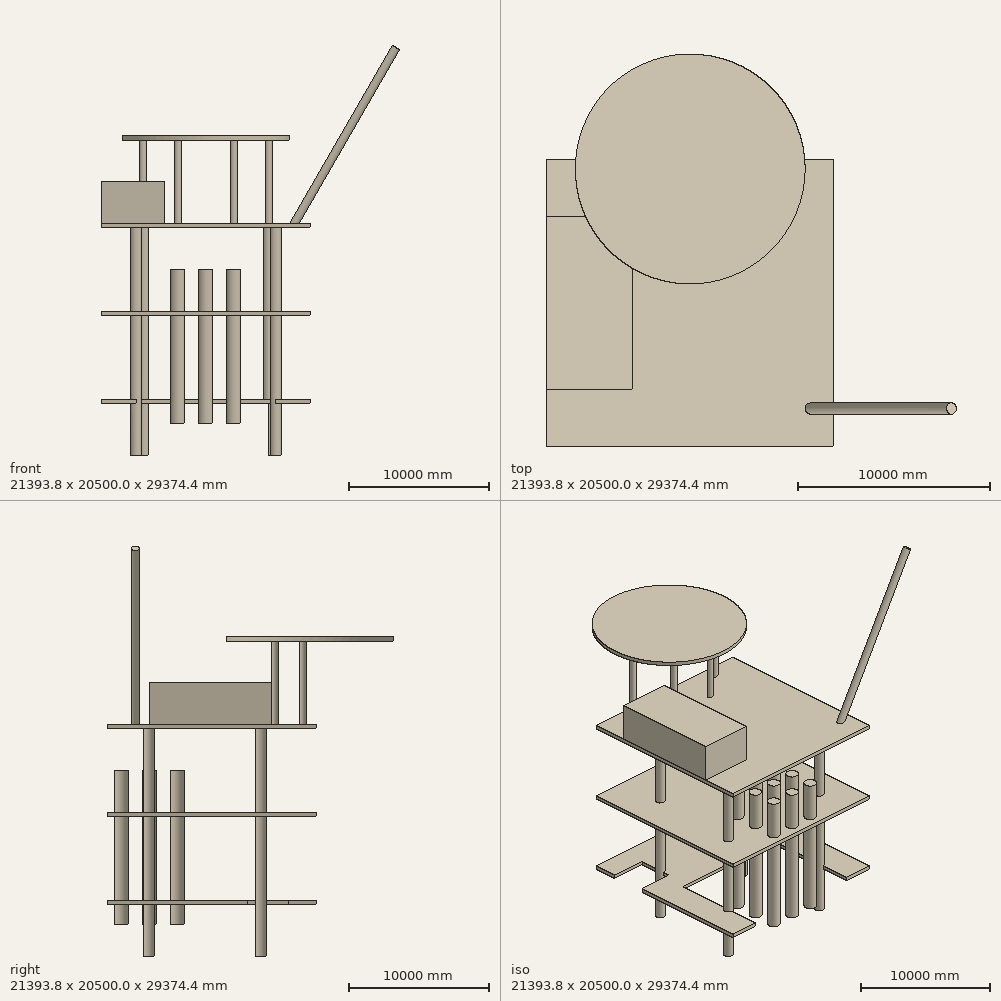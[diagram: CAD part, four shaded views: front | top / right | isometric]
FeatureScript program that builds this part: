
annotation { "Feature Type Name" : "Feature", "Feature Type Description" : "" }
export const myFeature = defineFeature(function(context is Context, id is Id, definition is map)
    precondition{}
    {
        {
            var Q0;
            Q0=qCreatedBy(makeId("Top.planeOp"),FACE);
            var sketch = newSketch(context, id + "F0", { "sketchPlane" : qUnion([Q0])});
            skLineSegment(sketch, "E0.bottom", {"start": v(-8810.08, 6724.82) * mm, "end": v(6189.92, 6724.82) * mm});
            skLineSegment(sketch, "E0.top", {"start": v(-8810.08, 21724.82) * mm, "end": v(6189.92, 21724.82) * mm});
            skLineSegment(sketch, "E0.left", {"start": v(-8810.08, 6724.82) * mm, "end": v(-8810.08, 21724.82) * mm});
            skLineSegment(sketch, "E0.right", {"start": v(6189.92, 6724.82) * mm, "end": v(6189.92, 21724.82) * mm});
            skSolve(sketch);
        }
        {
            var Q0;
            Q0 = qSketchRegion(id + "F0", true);
            extrude(context, id + "F1", {"entities" : qUnion([Q0]), "oppositeDirection" : true, "depth" : 300 * mm, "offsetDistance" : 25 * mm});
        }
        {
            var Q0;
            Q0=makeQuery(id+"F1.opExtrude","CAP_FACE",FACE,{"disambiguationData":[OSD([sQuery(id+"F0.wireOp",EDGE,"E0.bottom"),sQuery(id+"F0.wireOp",EDGE,"E0.top"),sQuery(id+"F0.wireOp",EDGE,"E0.left"),sQuery(id+"F0.wireOp",EDGE,"E0.right")])],"isStart":true});
            var sketch = newSketch(context, id + "F2", { "sketchPlane" : qUnion([Q0])});
            skLineSegment(sketch, "E1", {"start": v(-6310.08, 6724.82) * mm, "end": v(-6310.08, 14724.82) * mm});
            skLineSegment(sketch, "E2", {"start": v(-6310.08, 14724.82) * mm, "end": v(3689.92, 14724.82) * mm});
            skLineSegment(sketch, "E3", {"start": v(3689.92, 14724.82) * mm, "end": v(3689.92, 6724.82) * mm});
            skLineSegment(sketch, "E4", {"start": v(-1310.08, 6724.82) * mm, "end": v(-1310.08, 14724.82) * mm, "construction": true});
            skSolve(sketch);
        }
        {
            var Q0;
            Q0 = qSketchRegion(id + "F2", true);
            var Q1;
            {var subQ0=sQuery(id+"F2.wireOp",EDGE,"E1");Q1=makeQuery(id+"F2.imprint","IMPRINT",FACE,{"disambiguationData":[TD([[makeQuery(id+"F2.imprint","IMPRINT",EDGE,{"derivedFrom":subQ0}),-1.0]])]});}
            extrude(context, id + "F3", {"entities" : qUnion([Q0, Q1]), "operationType" : NewBodyOperationType.REMOVE, "endBound" : BoundingType.THROUGH_ALL, "oppositeDirection" : true, "depth" : 25 * mm, "offsetDistance" : 25 * mm});
        }
        {
            var Q0;
            Q0=makeQuery(id+"F1.opExtrude","CAP_FACE",FACE,{"disambiguationData":[OSD([sQuery(id+"F0.wireOp",EDGE,"E0.bottom"),sQuery(id+"F0.wireOp",EDGE,"E0.top"),sQuery(id+"F0.wireOp",EDGE,"E0.left"),sQuery(id+"F0.wireOp",EDGE,"E0.right")])],"isStart":true});
            var sketch = newSketch(context, id + "F4", { "sketchPlane" : qUnion([Q0])});
            skLineSegment(sketch, "E5", {"start": v(-8810.08, 19724.82) * mm, "end": v(-5810.08, 19724.82) * mm});
            skLineSegment(sketch, "E6", {"start": v(-5810.08, 19724.82) * mm, "end": v(-5810.08, 16724.82) * mm});
            skLineSegment(sketch, "E7", {"start": v(-5810.08, 16724.82) * mm, "end": v(-8810.08, 16724.82) * mm});
            skLineSegment(sketch, "E8", {"start": v(6189.92, 19724.82) * mm, "end": v(3189.92, 19724.82) * mm});
            skLineSegment(sketch, "E9", {"start": v(3189.92, 19724.82) * mm, "end": v(3189.92, 16724.82) * mm});
            skLineSegment(sketch, "E10", {"start": v(3189.92, 16724.82) * mm, "end": v(6189.92, 16724.82) * mm});
            skSolve(sketch);
        }
        {
            var Q0;
            {var subQ0=sQuery(id+"F4.wireOp",EDGE,"E5");Q0=makeQuery(id+"F4.imprint","IMPRINT",FACE,{"disambiguationData":[TD([[makeQuery(id+"F4.imprint","IMPRINT",EDGE,{"derivedFrom":subQ0}),-1.0]])]});}
            var Q1;
            {var subQ0=sQuery(id+"F4.wireOp",EDGE,"E8");Q1=makeQuery(id+"F4.imprint","IMPRINT",FACE,{"disambiguationData":[TD([[makeQuery(id+"F4.imprint","IMPRINT",EDGE,{"derivedFrom":subQ0}),1.0]])]});}
            extrude(context, id + "F5", {"entities" : qUnion([Q0, Q1]), "operationType" : NewBodyOperationType.REMOVE, "endBound" : BoundingType.THROUGH_ALL, "oppositeDirection" : true, "depth" : 25 * mm, "offsetDistance" : 25 * mm});
        }
        {
            var Q0;
            Q0=makeQuery(id+"F1.opExtrude","CAP_FACE",FACE,{"disambiguationData":[OSD([sQuery(id+"F0.wireOp",EDGE,"E0.bottom"),sQuery(id+"F0.wireOp",EDGE,"E0.top"),sQuery(id+"F0.wireOp",EDGE,"E0.left"),sQuery(id+"F0.wireOp",EDGE,"E0.right")])],"isStart":true});
            var sketch = newSketch(context, id + "F6", { "sketchPlane" : qUnion([Q0])});
            skCircle(sketch, "E11", {"center": v(-5810.08, 17724.82) * mm, "radius": 400 * mm});
            skCircle(sketch, "E12", {"center": v(3189.92, 17724.82) * mm, "radius": 400 * mm});
            skCircle(sketch, "E13", {"center": v(-6310.08, 9724.82) * mm, "radius": 400 * mm});
            skCircle(sketch, "E14", {"center": v(3689.92, 9724.82) * mm, "radius": 400 * mm});
            skSolve(sketch);
        }
        {
            var Q0;
            {var subQ0=sQuery(id+"F6.wireOp",EDGE,"E11");var subQ1=makeQuery(id+"F5.boolean.opBoolean","COPY",EDGE,{"derivedFrom":makeQuery(id+"F5.opExtrude","CAP_EDGE",EDGE,{"disambiguationData":[OSD([sQuery(id+"F4.wireOp",EDGE,"E6")])],"isStart":true})});var subQ2=makeQuery(id+"F6.imprint","INTERSECT",VERTEX,{"disambiguationData":[OD(0.0)],"derivedFrom":[subQ1,subQ0]});Q0=makeQuery(id+"F6.imprint","IMPRINT",FACE,{"disambiguationData":[TD([[makeQuery(id+"F6.imprint","IMPRINT",EDGE,{"disambiguationData":[TD([[subQ2,-1.0]])],"derivedFrom":subQ0}),1.0]])]});}
            var Q1;
            {var subQ0=sQuery(id+"F6.wireOp",EDGE,"E11");var subQ1=makeQuery(id+"F5.boolean.opBoolean","COPY",EDGE,{"derivedFrom":makeQuery(id+"F5.opExtrude","CAP_EDGE",EDGE,{"disambiguationData":[OSD([sQuery(id+"F4.wireOp",EDGE,"E6")])],"isStart":true})});var subQ2=makeQuery(id+"F6.imprint","INTERSECT",VERTEX,{"disambiguationData":[OD(0.0)],"derivedFrom":[subQ1,subQ0]});Q1=makeQuery(id+"F6.imprint","IMPRINT",FACE,{"disambiguationData":[TD([[makeQuery(id+"F6.imprint","IMPRINT",EDGE,{"disambiguationData":[TD([[subQ2,1.0]])],"derivedFrom":subQ0}),1.0]])]});}
            var Q2;
            {var subQ0=sQuery(id+"F6.wireOp",EDGE,"E13");var subQ1=makeQuery(id+"F3.boolean.opBoolean","COPY",EDGE,{"derivedFrom":makeQuery(id+"F3.opExtrude","CAP_EDGE",EDGE,{"disambiguationData":[OSD([sQuery(id+"F2.wireOp",EDGE,"E1")])],"isStart":true})});var subQ2=makeQuery(id+"F6.imprint","INTERSECT",VERTEX,{"disambiguationData":[OD(0.0)],"derivedFrom":[subQ1,subQ0]});Q2=makeQuery(id+"F6.imprint","IMPRINT",FACE,{"disambiguationData":[TD([[makeQuery(id+"F6.imprint","IMPRINT",EDGE,{"disambiguationData":[TD([[subQ2,-1.0]])],"derivedFrom":subQ0}),1.0]])]});}
            var Q3;
            {var subQ0=sQuery(id+"F6.wireOp",EDGE,"E13");var subQ1=makeQuery(id+"F3.boolean.opBoolean","COPY",EDGE,{"derivedFrom":makeQuery(id+"F3.opExtrude","CAP_EDGE",EDGE,{"disambiguationData":[OSD([sQuery(id+"F2.wireOp",EDGE,"E1")])],"isStart":true})});var subQ2=makeQuery(id+"F6.imprint","INTERSECT",VERTEX,{"disambiguationData":[OD(0.0)],"derivedFrom":[subQ1,subQ0]});Q3=makeQuery(id+"F6.imprint","IMPRINT",FACE,{"disambiguationData":[TD([[makeQuery(id+"F6.imprint","IMPRINT",EDGE,{"disambiguationData":[TD([[subQ2,1.0]])],"derivedFrom":subQ0}),1.0]])]});}
            var Q4;
            {var subQ0=sQuery(id+"F6.wireOp",EDGE,"E12");var subQ1=makeQuery(id+"F5.boolean.opBoolean","COPY",EDGE,{"derivedFrom":makeQuery(id+"F5.opExtrude","CAP_EDGE",EDGE,{"disambiguationData":[OSD([sQuery(id+"F4.wireOp",EDGE,"E9")])],"isStart":true})});var subQ2=makeQuery(id+"F6.imprint","INTERSECT",VERTEX,{"disambiguationData":[OD(0.0)],"derivedFrom":[subQ1,subQ0]});Q4=makeQuery(id+"F6.imprint","IMPRINT",FACE,{"disambiguationData":[TD([[makeQuery(id+"F6.imprint","IMPRINT",EDGE,{"disambiguationData":[TD([[subQ2,1.0]])],"derivedFrom":subQ0}),1.0]])]});}
            var Q5;
            {var subQ0=sQuery(id+"F6.wireOp",EDGE,"E12");var subQ1=makeQuery(id+"F5.boolean.opBoolean","COPY",EDGE,{"derivedFrom":makeQuery(id+"F5.opExtrude","CAP_EDGE",EDGE,{"disambiguationData":[OSD([sQuery(id+"F4.wireOp",EDGE,"E9")])],"isStart":true})});var subQ2=makeQuery(id+"F6.imprint","INTERSECT",VERTEX,{"disambiguationData":[OD(0.0)],"derivedFrom":[subQ1,subQ0]});Q5=makeQuery(id+"F6.imprint","IMPRINT",FACE,{"disambiguationData":[TD([[makeQuery(id+"F6.imprint","IMPRINT",EDGE,{"disambiguationData":[TD([[subQ2,-1.0]])],"derivedFrom":subQ0}),1.0]])]});}
            var Q6;
            {var subQ0=sQuery(id+"F6.wireOp",EDGE,"E14");var subQ1=makeQuery(id+"F3.boolean.opBoolean","COPY",EDGE,{"derivedFrom":makeQuery(id+"F3.opExtrude","CAP_EDGE",EDGE,{"disambiguationData":[OSD([sQuery(id+"F2.wireOp",EDGE,"E3")])],"isStart":true})});var subQ2=makeQuery(id+"F6.imprint","INTERSECT",VERTEX,{"disambiguationData":[OD(0.0)],"derivedFrom":[subQ1,subQ0]});Q6=makeQuery(id+"F6.imprint","IMPRINT",FACE,{"disambiguationData":[TD([[makeQuery(id+"F6.imprint","IMPRINT",EDGE,{"disambiguationData":[TD([[subQ2,-1.0]])],"derivedFrom":subQ0}),1.0]])]});}
            var Q7;
            {var subQ0=sQuery(id+"F6.wireOp",EDGE,"E14");var subQ1=makeQuery(id+"F3.boolean.opBoolean","COPY",EDGE,{"derivedFrom":makeQuery(id+"F3.opExtrude","CAP_EDGE",EDGE,{"disambiguationData":[OSD([sQuery(id+"F2.wireOp",EDGE,"E3")])],"isStart":true})});var subQ2=makeQuery(id+"F6.imprint","INTERSECT",VERTEX,{"disambiguationData":[OD(0.0)],"derivedFrom":[subQ1,subQ0]});Q7=makeQuery(id+"F6.imprint","IMPRINT",FACE,{"disambiguationData":[TD([[makeQuery(id+"F6.imprint","IMPRINT",EDGE,{"disambiguationData":[TD([[subQ2,1.0]])],"derivedFrom":subQ0}),1.0]])]});}
            extrude(context, id + "F7", {"entities" : qUnion([Q0, Q1, Q2, Q3, Q4, Q5, Q6, Q7]), "operationType" : NewBodyOperationType.ADD, "depth" : 6000 * mm, "offsetDistance" : 25 * mm});
        }
        {
            var Q0;
            Q0=makeQuery(id+"F7.opExtrude","CAP_FACE",FACE,{"disambiguationData":[OSD([sQuery(id+"F6.wireOp",EDGE,"E12")])],"isStart":true});
            var sketch = newSketch(context, id + "F8", { "sketchPlane" : qUnion([Q0])});
            skCircle(sketch, "E15", {"center": v(-6310.08, -9724.82) * mm, "radius": 400 * mm});
            skCircle(sketch, "E16", {"center": v(3689.92, -9724.82) * mm, "radius": 400 * mm});
            skCircle(sketch, "E17", {"center": v(-5810.08, -17724.82) * mm, "radius": 400 * mm});
            skCircle(sketch, "E18", {"center": v(3189.92, -17724.82) * mm, "radius": 400 * mm});
            skSolve(sketch);
        }
        {
            var Q0;
            Q0=makeQuery(id+"F8.imprint","IMPRINT",FACE,{"disambiguationData":[TD([[makeQuery(id+"F8.imprint","IMPRINT",EDGE,{"derivedFrom":sQuery(id+"F8.wireOp",EDGE,"E17")}),1.0]])]});
            var Q1;
            Q1=makeQuery(id+"F8.imprint","IMPRINT",FACE,{"disambiguationData":[TD([[makeQuery(id+"F8.imprint","IMPRINT",EDGE,{"disambiguationData":[OD(1.0)],"derivedFrom":sQuery(id+"F8.wireOp",EDGE,"E18")}),-1.0]])]});
            var Q2;
            Q2=makeQuery(id+"F8.imprint","IMPRINT",FACE,{"disambiguationData":[TD([[makeQuery(id+"F8.imprint","IMPRINT",EDGE,{"derivedFrom":sQuery(id+"F8.wireOp",EDGE,"E15")}),1.0]])]});
            var Q3;
            Q3=makeQuery(id+"F8.imprint","IMPRINT",FACE,{"disambiguationData":[TD([[makeQuery(id+"F8.imprint","IMPRINT",EDGE,{"derivedFrom":sQuery(id+"F8.wireOp",EDGE,"E16")}),1.0]])]});
            extrude(context, id + "F9", {"entities" : qUnion([Q0, Q1, Q2, Q3]), "operationType" : NewBodyOperationType.ADD, "depth" : 4000 * mm, "offsetDistance" : 25 * mm});
        }
        {
            var Q0;
            Q0=makeQuery(id+"F7.opExtrude","CAP_FACE",FACE,{"disambiguationData":[OSD([sQuery(id+"F6.wireOp",EDGE,"E11")])],"isStart":false});
            var sketch = newSketch(context, id + "F10", { "sketchPlane" : qUnion([Q0])});
            skLineSegment(sketch, "E19.bottom", {"start": v(-8810.08, 21724.82) * mm, "end": v(6189.92, 21724.82) * mm});
            skLineSegment(sketch, "E19.top", {"start": v(-8810.08, 6724.82) * mm, "end": v(6189.92, 6724.82) * mm});
            skLineSegment(sketch, "E19.left", {"start": v(-8810.08, 21724.82) * mm, "end": v(-8810.08, 6724.82) * mm});
            skLineSegment(sketch, "E19.right", {"start": v(6189.92, 21724.82) * mm, "end": v(6189.92, 6724.82) * mm});
            skSolve(sketch);
        }
        {
            var Q0;
            Q0=makeQuery(id+"F10.imprint","IMPRINT",FACE,{"disambiguationData":[TD([[makeQuery(id+"F10.imprint","IMPRINT",EDGE,{"derivedFrom":sQuery(id+"F10.wireOp",EDGE,"E19.bottom")}),-1.0]])]});
            var Q1;
            Q1=makeQuery(id+"F10.imprint","IMPRINT",FACE,{"disambiguationData":[TD([[makeQuery(id+"F10.imprint","IMPRINT",EDGE,{"derivedFrom":makeQuery(id+"F7.opExtrude","CAP_EDGE",EDGE,{"disambiguationData":[OSD([sQuery(id+"F6.wireOp",EDGE,"E11")])],"isStart":false})}),1.0]])]});
            extrude(context, id + "F11", {"entities" : qUnion([Q0, Q1]), "operationType" : NewBodyOperationType.ADD, "depth" : 300 * mm, "offsetDistance" : 25 * mm});
        }
        {
            var Q0;
            Q0=makeQuery(id+"F11.opExtrude","CAP_FACE",FACE,{"disambiguationData":[OSD([sQuery(id+"F10.wireOp",EDGE,"E19.bottom"),sQuery(id+"F10.wireOp",EDGE,"E19.top"),sQuery(id+"F10.wireOp",EDGE,"E19.left"),sQuery(id+"F10.wireOp",EDGE,"E19.right")])],"isStart":false});
            var sketch = newSketch(context, id + "F12", { "sketchPlane" : qUnion([Q0])});
            skCircle(sketch, "E20", {"center": v(-3310.08, 7724.82) * mm, "radius": 500 * mm});
            skCircle(sketch, "E21", {"center": v(-1310.08, 7724.82) * mm, "radius": 500 * mm});
            skCircle(sketch, "E22", {"center": v(689.92, 7724.82) * mm, "radius": 500 * mm});
            skCircle(sketch, "E23", {"center": v(-3310.08, 9724.82) * mm, "radius": 500 * mm});
            skCircle(sketch, "E24", {"center": v(-1310.08, 9724.82) * mm, "radius": 500 * mm});
            skCircle(sketch, "E25", {"center": v(689.92, 9724.82) * mm, "radius": 500 * mm});
            skCircle(sketch, "E26", {"center": v(-3310.08, 11724.82) * mm, "radius": 500 * mm});
            skCircle(sketch, "E27", {"center": v(-1310.08, 11724.82) * mm, "radius": 500 * mm});
            skCircle(sketch, "E28", {"center": v(689.92, 11724.82) * mm, "radius": 500 * mm});
            skSolve(sketch);
        }
        {
            var Q0;
            Q0=makeQuery(id+"F12.imprint","IMPRINT",FACE,{"disambiguationData":[TD([[makeQuery(id+"F12.imprint","IMPRINT",EDGE,{"derivedFrom":sQuery(id+"F12.wireOp",EDGE,"E20")}),1.0]])]});
            var Q1;
            Q1=makeQuery(id+"F12.imprint","IMPRINT",FACE,{"disambiguationData":[TD([[makeQuery(id+"F12.imprint","IMPRINT",EDGE,{"derivedFrom":sQuery(id+"F12.wireOp",EDGE,"E23")}),1.0]])]});
            var Q2;
            Q2=makeQuery(id+"F12.imprint","IMPRINT",FACE,{"disambiguationData":[TD([[makeQuery(id+"F12.imprint","IMPRINT",EDGE,{"derivedFrom":sQuery(id+"F12.wireOp",EDGE,"E26")}),1.0]])]});
            var Q3;
            Q3=makeQuery(id+"F12.imprint","IMPRINT",FACE,{"disambiguationData":[TD([[makeQuery(id+"F12.imprint","IMPRINT",EDGE,{"derivedFrom":sQuery(id+"F12.wireOp",EDGE,"E27")}),1.0]])]});
            var Q4;
            Q4=makeQuery(id+"F12.imprint","IMPRINT",FACE,{"disambiguationData":[TD([[makeQuery(id+"F12.imprint","IMPRINT",EDGE,{"derivedFrom":sQuery(id+"F12.wireOp",EDGE,"E28")}),1.0]])]});
            var Q5;
            Q5=makeQuery(id+"F12.imprint","IMPRINT",FACE,{"disambiguationData":[TD([[makeQuery(id+"F12.imprint","IMPRINT",EDGE,{"derivedFrom":sQuery(id+"F12.wireOp",EDGE,"E25")}),1.0]])]});
            var Q6;
            Q6=makeQuery(id+"F12.imprint","IMPRINT",FACE,{"disambiguationData":[TD([[makeQuery(id+"F12.imprint","IMPRINT",EDGE,{"derivedFrom":sQuery(id+"F12.wireOp",EDGE,"E22")}),1.0]])]});
            var Q7;
            Q7=makeQuery(id+"F12.imprint","IMPRINT",FACE,{"disambiguationData":[TD([[makeQuery(id+"F12.imprint","IMPRINT",EDGE,{"derivedFrom":sQuery(id+"F12.wireOp",EDGE,"E21")}),1.0]])]});
            var Q8;
            Q8=makeQuery(id+"F12.imprint","IMPRINT",FACE,{"disambiguationData":[TD([[makeQuery(id+"F12.imprint","IMPRINT",EDGE,{"derivedFrom":sQuery(id+"F12.wireOp",EDGE,"E24")}),1.0]])]});
            extrude(context, id + "F13", {"entities" : qUnion([Q0, Q1, Q2, Q3, Q4, Q5, Q6, Q7, Q8]), "oppositeDirection" : true, "depth" : 8000 * mm, "offsetDistance" : 25 * mm});
        }
        {
            var Q0;
            Q0=makeQuery(id+"F13.opExtrude","CAP_FACE",FACE,{"disambiguationData":[OSD([sQuery(id+"F12.wireOp",EDGE,"E20")])],"isStart":true});
            var Q1;
            Q1=makeQuery(id+"F13.opExtrude","CAP_FACE",FACE,{"disambiguationData":[OSD([sQuery(id+"F12.wireOp",EDGE,"E23")])],"isStart":true});
            var Q2;
            Q2=makeQuery(id+"F13.opExtrude","CAP_FACE",FACE,{"disambiguationData":[OSD([sQuery(id+"F12.wireOp",EDGE,"E26")])],"isStart":true});
            var Q3;
            Q3=makeQuery(id+"F13.opExtrude","CAP_FACE",FACE,{"disambiguationData":[OSD([sQuery(id+"F12.wireOp",EDGE,"E27")])],"isStart":true});
            var Q4;
            Q4=makeQuery(id+"F13.opExtrude","CAP_FACE",FACE,{"disambiguationData":[OSD([sQuery(id+"F12.wireOp",EDGE,"E24")])],"isStart":true});
            var Q5;
            Q5=makeQuery(id+"F13.opExtrude","CAP_FACE",FACE,{"disambiguationData":[OSD([sQuery(id+"F12.wireOp",EDGE,"E21")])],"isStart":true});
            var Q6;
            Q6=makeQuery(id+"F13.opExtrude","CAP_FACE",FACE,{"disambiguationData":[OSD([sQuery(id+"F12.wireOp",EDGE,"E22")])],"isStart":true});
            var Q7;
            Q7=makeQuery(id+"F13.opExtrude","CAP_FACE",FACE,{"disambiguationData":[OSD([sQuery(id+"F12.wireOp",EDGE,"E25")])],"isStart":true});
            var Q8;
            Q8=makeQuery(id+"F13.opExtrude","CAP_FACE",FACE,{"disambiguationData":[OSD([sQuery(id+"F12.wireOp",EDGE,"E28")])],"isStart":true});
            extrude(context, id + "F14", {"entities" : qUnion([Q0, Q1, Q2, Q3, Q4, Q5, Q6, Q7, Q8]), "depth" : 3000 * mm, "offsetDistance" : 25 * mm});
        }
        {
            var Q0;
            Q0=makeQuery(id+"F12.imprint","IMPRINT",FACE,{"disambiguationData":[TD([[makeQuery(id+"F12.imprint","IMPRINT",EDGE,{"derivedFrom":sQuery(id+"F12.wireOp",EDGE,"E20")}),-1.0]])]});
            var sketch = newSketch(context, id + "F15", { "sketchPlane" : qUnion([Q0])});
            skCircle(sketch, "E29", {"center": v(-5810.08, 17724.82) * mm, "radius": 400 * mm});
            skCircle(sketch, "E30", {"center": v(3189.92, 17724.82) * mm, "radius": 400 * mm});
            skCircle(sketch, "E31", {"center": v(-6310.08, 9724.82) * mm, "radius": 400 * mm});
            skCircle(sketch, "E32", {"center": v(3689.92, 9724.82) * mm, "radius": 400 * mm});
            skSolve(sketch);
        }
        {
            var Q0;
            Q0=makeQuery(id+"F15.imprint","IMPRINT",FACE,{"disambiguationData":[TD([[makeQuery(id+"F15.imprint","IMPRINT",EDGE,{"derivedFrom":sQuery(id+"F15.wireOp",EDGE,"E29")}),1.0]])]});
            var Q1;
            Q1=makeQuery(id+"F15.imprint","IMPRINT",FACE,{"disambiguationData":[TD([[makeQuery(id+"F15.imprint","IMPRINT",EDGE,{"derivedFrom":sQuery(id+"F15.wireOp",EDGE,"E30")}),1.0]])]});
            var Q2;
            Q2=makeQuery(id+"F15.imprint","IMPRINT",FACE,{"disambiguationData":[TD([[makeQuery(id+"F15.imprint","IMPRINT",EDGE,{"derivedFrom":sQuery(id+"F15.wireOp",EDGE,"E31")}),1.0]])]});
            var Q3;
            Q3=makeQuery(id+"F15.imprint","IMPRINT",FACE,{"disambiguationData":[TD([[makeQuery(id+"F15.imprint","IMPRINT",EDGE,{"derivedFrom":sQuery(id+"F15.wireOp",EDGE,"E32")}),1.0]])]});
            extrude(context, id + "F16", {"entities" : qUnion([Q0, Q1, Q2, Q3]), "operationType" : NewBodyOperationType.ADD, "depth" : 6000 * mm, "offsetDistance" : 25 * mm});
        }
        {
            var Q0;
            Q0=makeQuery(id+"F16.opExtrude","CAP_FACE",FACE,{"disambiguationData":[OSD([sQuery(id+"F15.wireOp",EDGE,"E31")])],"isStart":false});
            var sketch = newSketch(context, id + "F17", { "sketchPlane" : qUnion([Q0])});
            skLineSegment(sketch, "E33.bottom", {"start": v(-8810.08, 21724.82) * mm, "end": v(6189.92, 21724.82) * mm});
            skLineSegment(sketch, "E33.top", {"start": v(-8810.08, 6724.82) * mm, "end": v(6189.92, 6724.82) * mm});
            skLineSegment(sketch, "E33.left", {"start": v(-8810.08, 21724.82) * mm, "end": v(-8810.08, 6724.82) * mm});
            skLineSegment(sketch, "E33.right", {"start": v(6189.92, 21724.82) * mm, "end": v(6189.92, 6724.82) * mm});
            skSolve(sketch);
        }
        {
            var Q0;
            Q0=makeQuery(id+"F17.imprint","IMPRINT",FACE,{"disambiguationData":[TD([[makeQuery(id+"F17.imprint","IMPRINT",EDGE,{"derivedFrom":sQuery(id+"F17.wireOp",EDGE,"E33.bottom")}),-1.0]])]});
            var Q1;
            Q1=makeQuery(id+"F17.imprint","IMPRINT",FACE,{"disambiguationData":[TD([[makeQuery(id+"F17.imprint","IMPRINT",EDGE,{"derivedFrom":makeQuery(id+"F16.opExtrude","CAP_EDGE",EDGE,{"disambiguationData":[OSD([sQuery(id+"F15.wireOp",EDGE,"E31")])],"isStart":false})}),1.0]])]});
            extrude(context, id + "F18", {"entities" : qUnion([Q0, Q1]), "operationType" : NewBodyOperationType.ADD, "depth" : 300 * mm, "offsetDistance" : 25 * mm});
        }
        {
            var Q0;
            Q0=makeQuery(id+"F18.opExtrude","CAP_FACE",FACE,{"disambiguationData":[OSD([sQuery(id+"F17.wireOp",EDGE,"E33.bottom"),sQuery(id+"F17.wireOp",EDGE,"E33.top"),sQuery(id+"F17.wireOp",EDGE,"E33.left"),sQuery(id+"F17.wireOp",EDGE,"E33.right")])],"isStart":false});
            var sketch = newSketch(context, id + "F19", { "sketchPlane" : qUnion([Q0])});
            skLineSegment(sketch, "E34.bottom", {"start": v(-8810.08, 18724.82) * mm, "end": v(-4310.08, 18724.82) * mm});
            skLineSegment(sketch, "E34.top", {"start": v(-8810.08, 9724.82) * mm, "end": v(-4310.08, 9724.82) * mm});
            skLineSegment(sketch, "E34.left", {"start": v(-8810.08, 18724.82) * mm, "end": v(-8810.08, 9724.82) * mm});
            skLineSegment(sketch, "E34.right", {"start": v(-4310.08, 18724.82) * mm, "end": v(-4310.08, 9724.82) * mm});
            skCircle(sketch, "E35", {"center": v(-3310.08, 18724.82) * mm, "radius": 250 * mm});
            skCircle(sketch, "E36", {"center": v(689.92, 18724.82) * mm, "radius": 250 * mm});
            skSolve(sketch);
        }
        {
            var Q0;
            Q0=makeQuery(id+"F19.imprint","IMPRINT",FACE,{"disambiguationData":[TD([[makeQuery(id+"F19.imprint","IMPRINT",EDGE,{"derivedFrom":sQuery(id+"F19.wireOp",EDGE,"E34.bottom")}),-1.0]])]});
            extrude(context, id + "F20", {"entities" : qUnion([Q0]), "depth" : 3000 * mm, "offsetDistance" : 25 * mm});
        }
        {
            var Q0;
            Q0=makeQuery(id+"F18.opExtrude","CAP_FACE",FACE,{"disambiguationData":[OSD([sQuery(id+"F17.wireOp",EDGE,"E33.bottom"),sQuery(id+"F17.wireOp",EDGE,"E33.top"),sQuery(id+"F17.wireOp",EDGE,"E33.left"),sQuery(id+"F17.wireOp",EDGE,"E33.right")])],"isStart":false});
            var sketch = newSketch(context, id + "F21", { "sketchPlane" : qUnion([Q0])});
            skCircle(sketch, "E37", {"center": v(-3310.08, 18724.82) * mm, "radius": 250 * mm});
            skCircle(sketch, "E38", {"center": v(689.92, 18724.82) * mm, "radius": 250 * mm});
            skCircle(sketch, "E39", {"center": v(-5810.08, 20724.82) * mm, "radius": 250 * mm});
            skCircle(sketch, "E40", {"center": v(3189.92, 20724.82) * mm, "radius": 250 * mm});
            skSolve(sketch);
        }
        {
            var Q0;
            Q0=makeQuery(id+"F21.imprint","IMPRINT",FACE,{"disambiguationData":[TD([[makeQuery(id+"F21.imprint","IMPRINT",EDGE,{"derivedFrom":sQuery(id+"F21.wireOp",EDGE,"E39")}),1.0]])]});
            var Q1;
            Q1=makeQuery(id+"F21.imprint","IMPRINT",FACE,{"disambiguationData":[TD([[makeQuery(id+"F21.imprint","IMPRINT",EDGE,{"derivedFrom":sQuery(id+"F21.wireOp",EDGE,"E37")}),1.0]])]});
            var Q2;
            Q2=makeQuery(id+"F21.imprint","IMPRINT",FACE,{"disambiguationData":[TD([[makeQuery(id+"F21.imprint","IMPRINT",EDGE,{"derivedFrom":sQuery(id+"F21.wireOp",EDGE,"E38")}),1.0]])]});
            var Q3;
            Q3=makeQuery(id+"F21.imprint","IMPRINT",FACE,{"disambiguationData":[TD([[makeQuery(id+"F21.imprint","IMPRINT",EDGE,{"derivedFrom":sQuery(id+"F21.wireOp",EDGE,"E40")}),1.0]])]});
            extrude(context, id + "F22", {"entities" : qUnion([Q0, Q1, Q2, Q3]), "operationType" : NewBodyOperationType.ADD, "depth" : 6000 * mm, "offsetDistance" : 25 * mm});
        }
        {
            var Q0;
            Q0=makeQuery(id+"F22.opExtrude","CAP_FACE",FACE,{"disambiguationData":[OSD([sQuery(id+"F21.wireOp",EDGE,"E37")])],"isStart":false});
            var sketch = newSketch(context, id + "F23", { "sketchPlane" : qUnion([Q0])});
            skCircle(sketch, "E41", {"center": v(-1310.08, 21224.82) * mm, "radius": 6000 * mm});
            skSolve(sketch);
        }
        {
            var Q0;
            Q0=makeQuery(id+"F23.imprint","IMPRINT",FACE,{"disambiguationData":[TD([[makeQuery(id+"F23.imprint","IMPRINT",EDGE,{"derivedFrom":sQuery(id+"F23.wireOp",EDGE,"E41")}),1.0]])]});
            var Q1;
            Q1=makeQuery(id+"F23.imprint","IMPRINT",FACE,{"disambiguationData":[TD([[makeQuery(id+"F23.imprint","IMPRINT",EDGE,{"derivedFrom":makeQuery(id+"F22.opExtrude","CAP_EDGE",EDGE,{"disambiguationData":[OSD([sQuery(id+"F21.wireOp",EDGE,"E37")])],"isStart":false})}),1.0]])]});
            extrude(context, id + "F24", {"entities" : qUnion([Q0, Q1]), "operationType" : NewBodyOperationType.ADD, "depth" : 300 * mm, "offsetDistance" : 25 * mm});
        }
        {
            var Q0;
            Q0=makeQuery(id+"F18.opExtrude","CAP_FACE",FACE,{"disambiguationData":[OSD([sQuery(id+"F17.wireOp",EDGE,"E33.bottom"),sQuery(id+"F17.wireOp",EDGE,"E33.top"),sQuery(id+"F17.wireOp",EDGE,"E33.left"),sQuery(id+"F17.wireOp",EDGE,"E33.right")])],"isStart":false});
            var sketch = newSketch(context, id + "F25", { "sketchPlane" : qUnion([Q0])});
            skCircle(sketch, "E42", {"center": v(5189.92, 8724.82) * mm, "radius": 300 * mm});
            skSolve(sketch);
        }
        {
            var Q0;
            Q0=makeQuery(id+"F25.imprint","IMPRINT",FACE,{"disambiguationData":[TD([[makeQuery(id+"F25.imprint","IMPRINT",EDGE,{"derivedFrom":sQuery(id+"F25.wireOp",EDGE,"E42")}),1.0]])]});
            extrude(context, id + "F26", {"entities" : qUnion([Q0]), "depth" : 14000 * mm, "offsetDistance" : 25 * mm});
        }
        {
            var Q0;
            Q0=makeQuery(id+"F26.opExtrude","SWEPT_BODY",BODY,{"disambiguationData":[OSD([sQuery(id+"F25.wireOp",EDGE,"E42")])]});
            var Q1;
            Q1=makeQuery(id+"F18.opExtrude","CAP_EDGE",EDGE,{"disambiguationData":[OSD([sQuery(id+"F17.wireOp",EDGE,"E33.right")])],"isStart":false});
            transform(context, id + "F27", {"entities" : qUnion([Q0]), "transformType" : TransformType.ROTATION, "transformAxis" : qUnion([Q1]), "angle" : 30 * degree, "oppositeDirection" : true, "makeCopy" : false});
        }
        {
            var Q0;
            Q0=makeQuery(id+"F26.opExtrude","CAP_FACE",FACE,{"disambiguationData":[OSD([sQuery(id+"F25.wireOp",EDGE,"E42")])],"isStart":true});
            var sketch = newSketch(context, id + "F28", { "sketchPlane" : qUnion([Q0])});
            skCircle(sketch, "E43", {"center": v(-1939.37, -8724.82) * mm, "radius": 300 * mm});
            skSolve(sketch);
        }
        {
            var Q0;
            Q0=makeQuery(id+"F28.imprint","IMPRINT",FACE,{"disambiguationData":[TD([[makeQuery(id+"F28.imprint","IMPRINT",EDGE,{"derivedFrom":sQuery(id+"F28.wireOp",EDGE,"E43")}),-1.0]])]});
            extrude(context, id + "F29", {"entities" : qUnion([Q0]), "operationType" : NewBodyOperationType.ADD, "endBound" : BoundingType.UP_TO_NEXT, "depth" : 25 * mm, "offsetDistance" : 25 * mm});
        }
    });
